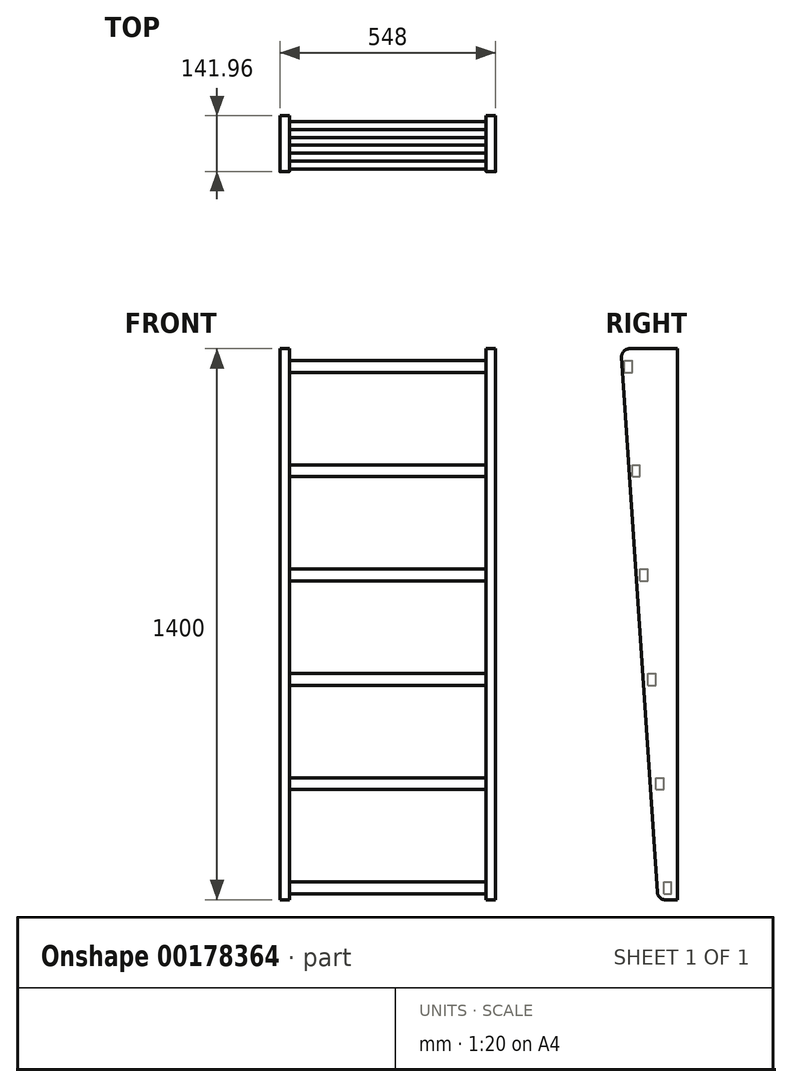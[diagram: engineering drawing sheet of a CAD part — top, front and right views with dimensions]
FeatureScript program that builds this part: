
annotation { "Feature Type Name" : "Feature", "Feature Type Description" : "" }
export const myFeature = defineFeature(function(context is Context, id is Id, definition is map)
    precondition{}
    {
        {
            var Q0;
            Q0=qCreatedBy(makeId("Top.planeOp"),FACE);
            var sketch = newSketch(context, id + "F0", { "sketchPlane" : qUnion([Q0])});
            skLineSegment(sketch, "E0.bottom", {"start": v(-250, -75) * mm, "end": v(-274, -75) * mm});
            skLineSegment(sketch, "E0.top", {"start": v(-250, 75) * mm, "end": v(-274, 75) * mm});
            skLineSegment(sketch, "E0.left", {"start": v(-250, -75) * mm, "end": v(-250, 75) * mm});
            skLineSegment(sketch, "E0.right", {"start": v(-274, -75) * mm, "end": v(-274, 75) * mm});
            skPoint(sketch, "E0.middle", {"position": v(-262, 0) * mm});
            skLineSegment(sketch, "E1.MirrorCS", {"start": v(250, -75) * mm, "end": v(274, -75) * mm});
            skPoint(sketch, "E2.MirrorP", {"position": v(262, 0) * mm});
            skLineSegment(sketch, "E3.MirrorCS", {"start": v(274, -75) * mm, "end": v(274, 75) * mm});
            skLineSegment(sketch, "E4.MirrorCS", {"start": v(250, -75) * mm, "end": v(250, 75) * mm});
            skLineSegment(sketch, "E5.MirrorCS", {"start": v(250, 75) * mm, "end": v(274, 75) * mm});
            skSolve(sketch);
        }
        {
            var Q0;
            Q0 = qSketchRegion(id + "F0", true);
            extrude(context, id + "F1", {"entities" : qUnion([Q0]), "depth" : 1400 * mm});
        }
        {
            var Q0;
            Q0=makeQuery(id+"F1.opExtrude","SWEPT_FACE",FACE,{"disambiguationData":[OSD([sQuery(id+"F0.wireOp",EDGE,"E4.MirrorCS")])]});
            var sketch = newSketch(context, id + "F2", { "sketchPlane" : qUnion([Q0])});
            skPoint(sketch, "E6.centerSnap0", {"position": v(0, 1400) * mm});
            skLineSegment(sketch, "E7.bottom", {"start": v(10, 1340) * mm, "end": v(-10, 1340) * mm});
            skLineSegment(sketch, "E7.top", {"start": v(10, 1370) * mm, "end": v(-10, 1370) * mm});
            skLineSegment(sketch, "E7.left", {"start": v(10, 1340) * mm, "end": v(10, 1370) * mm});
            skLineSegment(sketch, "E7.right", {"start": v(-10, 1340) * mm, "end": v(-10, 1370) * mm});
            skPoint(sketch, "E7.middle", {"position": v(0, 1355) * mm});
            skLineSegment(sketch, "E8.0.1.0", {"start": v(10, 1075) * mm, "end": v(10, 1105) * mm});
            skLineSegment(sketch, "E8.0.1.1", {"start": v(-10, 1075) * mm, "end": v(-10, 1105) * mm});
            skPoint(sketch, "E8.0.1.2", {"position": v(0, 1090) * mm});
            skLineSegment(sketch, "E8.0.1.3", {"start": v(10, 1105) * mm, "end": v(-10, 1105) * mm});
            skLineSegment(sketch, "E8.0.1.4", {"start": v(10, 1075) * mm, "end": v(-10, 1075) * mm});
            skLineSegment(sketch, "E8.0.2.0", {"start": v(10, 810) * mm, "end": v(10, 840) * mm});
            skLineSegment(sketch, "E8.0.2.1", {"start": v(-10, 810) * mm, "end": v(-10, 840) * mm});
            skPoint(sketch, "E8.0.2.2", {"position": v(0, 825) * mm});
            skLineSegment(sketch, "E8.0.2.3", {"start": v(10, 840) * mm, "end": v(-10, 840) * mm});
            skLineSegment(sketch, "E8.0.2.4", {"start": v(10, 810) * mm, "end": v(-10, 810) * mm});
            skLineSegment(sketch, "E8.0.3.0", {"start": v(10, 545) * mm, "end": v(10, 575) * mm});
            skLineSegment(sketch, "E8.0.3.1", {"start": v(-10, 545) * mm, "end": v(-10, 575) * mm});
            skPoint(sketch, "E8.0.3.2", {"position": v(0, 560) * mm});
            skLineSegment(sketch, "E8.0.3.3", {"start": v(10, 575) * mm, "end": v(-10, 575) * mm});
            skLineSegment(sketch, "E8.0.3.4", {"start": v(10, 545) * mm, "end": v(-10, 545) * mm});
            skLineSegment(sketch, "E8.0.4.0", {"start": v(10, 280) * mm, "end": v(10, 310) * mm});
            skLineSegment(sketch, "E8.0.4.1", {"start": v(-10, 280) * mm, "end": v(-10, 310) * mm});
            skPoint(sketch, "E8.0.4.2", {"position": v(0, 295) * mm});
            skLineSegment(sketch, "E8.0.4.3", {"start": v(10, 310) * mm, "end": v(-10, 310) * mm});
            skLineSegment(sketch, "E8.0.4.4", {"start": v(10, 280) * mm, "end": v(-10, 280) * mm});
            skLineSegment(sketch, "E8.direction1", {"start": v(-10, 1340) * mm, "end": v(21, 1340) * mm, "construction": true});
            skLineSegment(sketch, "E8.direction2", {"start": v(-10, 1340) * mm, "end": v(-10, 1075) * mm, "construction": true});
            skLineSegment(sketch, "E9.0.0.5", {"start": v(10, 15) * mm, "end": v(10, 45) * mm});
            skLineSegment(sketch, "E9.3.0.5", {"start": v(-10, 15) * mm, "end": v(-10, 45) * mm});
            skPoint(sketch, "E9.6.0.5", {"position": v(0, 30) * mm});
            skLineSegment(sketch, "E9.7.0.5", {"start": v(10, 45) * mm, "end": v(-10, 45) * mm});
            skLineSegment(sketch, "E9.10.0.5", {"start": v(10, 15) * mm, "end": v(-10, 15) * mm});
            skSolve(sketch);
        }
        {
            var Q0;
            Q0=makeQuery(id+"F2.imprint","IMPRINT",FACE,{"disambiguationData":[TD([[makeQuery(id+"F2.imprint","IMPRINT",EDGE,{"derivedFrom":sQuery(id+"F2.wireOp",EDGE,"E7.bottom")}),-1.0]])]});
            var Q1;
            Q1=makeQuery(id+"F2.imprint","IMPRINT",FACE,{"disambiguationData":[TD([[makeQuery(id+"F2.imprint","IMPRINT",EDGE,{"derivedFrom":sQuery(id+"F2.wireOp",EDGE,"E8.0.1.0")}),1.0]])]});
            var Q2;
            Q2=makeQuery(id+"F2.imprint","IMPRINT",FACE,{"disambiguationData":[TD([[makeQuery(id+"F2.imprint","IMPRINT",EDGE,{"derivedFrom":sQuery(id+"F2.wireOp",EDGE,"E8.0.2.0")}),1.0]])]});
            var Q3;
            Q3=makeQuery(id+"F2.imprint","IMPRINT",FACE,{"disambiguationData":[TD([[makeQuery(id+"F2.imprint","IMPRINT",EDGE,{"derivedFrom":sQuery(id+"F2.wireOp",EDGE,"E8.0.3.0")}),1.0]])]});
            var Q4;
            Q4=makeQuery(id+"F2.imprint","IMPRINT",FACE,{"disambiguationData":[TD([[makeQuery(id+"F2.imprint","IMPRINT",EDGE,{"derivedFrom":sQuery(id+"F2.wireOp",EDGE,"E9.0.0.5")}),1.0]])]});
            var Q5;
            Q5=makeQuery(id+"F2.imprint","IMPRINT",FACE,{"disambiguationData":[TD([[makeQuery(id+"F2.imprint","IMPRINT",EDGE,{"derivedFrom":sQuery(id+"F2.wireOp",EDGE,"E8.0.4.0")}),1.0]])]});
            extrude(context, id + "F3", {"entities" : qUnion([Q0, Q1, Q2, Q3, Q4, Q5]), "endBound" : BoundingType.UP_TO_NEXT, "depth" : 25 * mm});
        }
        {
            var Q0;
            Q0=makeQuery(id+"F1.opExtrude","CAP_EDGE",EDGE,{"disambiguationData":[OSD([sQuery(id+"F0.wireOp",EDGE,"E0.bottom")])],"isStart":true});
            chamfer(context, id + "F4", {"entities" : qUnion([Q0]), "chamferType" : ChamferType.TWO_OFFSETS, "width1" : 100 * mm, "oppositeDirection" : false, "width2" : 1500 * mm, "tangentPropagation" : true});
        }
        {
            var Q0;
            Q0=makeQuery(id+"F1.opExtrude","CAP_EDGE",EDGE,{"disambiguationData":[OSD([sQuery(id+"F0.wireOp",EDGE,"E1.MirrorCS")])],"isStart":true});
            chamfer(context, id + "F5", {"entities" : qUnion([Q0]), "chamferType" : ChamferType.TWO_OFFSETS, "width1" : 1500 * mm, "oppositeDirection" : false, "width2" : 100 * mm, "tangentPropagation" : true});
        }
        {
            var Q0;
            Q0=makeQuery(id+"F3.opExtrude","SWEPT_BODY",BODY,{"disambiguationData":[OSD([sQuery(id+"F2.wireOp",EDGE,"E7.bottom"),sQuery(id+"F2.wireOp",EDGE,"E7.top"),sQuery(id+"F2.wireOp",EDGE,"E7.left"),sQuery(id+"F2.wireOp",EDGE,"E7.right")])]});
            transform(context, id + "F6", {"entities" : qUnion([Q0]), "transformType" : TransformType.TRANSLATION_3D, "dx" : 0 * mm, "dy" : -50 * mm, "dz" : 0 * mm, "makeCopy" : false});
        }
        {
            var Q0;
            Q0=makeQuery(id+"F3.opExtrude","SWEPT_BODY",BODY,{"disambiguationData":[OSD([sQuery(id+"F2.wireOp",EDGE,"E8.0.1.0"),sQuery(id+"F2.wireOp",EDGE,"E8.0.1.1"),sQuery(id+"F2.wireOp",EDGE,"E8.0.1.3"),sQuery(id+"F2.wireOp",EDGE,"E8.0.1.4")])]});
            transform(context, id + "F7", {"entities" : qUnion([Q0]), "transformType" : TransformType.TRANSLATION_3D, "dx" : 0 * mm, "dy" : -30 * mm, "dz" : 0 * mm, "makeCopy" : false});
        }
        {
            var Q0;
            Q0=makeQuery(id+"F3.opExtrude","SWEPT_BODY",BODY,{"disambiguationData":[OSD([sQuery(id+"F2.wireOp",EDGE,"E8.0.2.0"),sQuery(id+"F2.wireOp",EDGE,"E8.0.2.1"),sQuery(id+"F2.wireOp",EDGE,"E8.0.2.3"),sQuery(id+"F2.wireOp",EDGE,"E8.0.2.4")])]});
            transform(context, id + "F8", {"entities" : qUnion([Q0]), "transformType" : TransformType.TRANSLATION_3D, "dx" : 0 * mm, "dy" : -10 * mm, "dz" : 0 * mm, "makeCopy" : false});
        }
        {
            var Q0;
            Q0=makeQuery(id+"F3.opExtrude","SWEPT_BODY",BODY,{"disambiguationData":[OSD([sQuery(id+"F2.wireOp",EDGE,"E8.0.3.0"),sQuery(id+"F2.wireOp",EDGE,"E8.0.3.1"),sQuery(id+"F2.wireOp",EDGE,"E8.0.3.3"),sQuery(id+"F2.wireOp",EDGE,"E8.0.3.4")])]});
            transform(context, id + "F9", {"entities" : qUnion([Q0]), "transformType" : TransformType.TRANSLATION_3D, "dx" : 0 * mm, "dy" : 10 * mm, "dz" : 0 * mm, "makeCopy" : false});
        }
        {
            var Q0;
            Q0=makeQuery(id+"F3.opExtrude","SWEPT_BODY",BODY,{"disambiguationData":[OSD([sQuery(id+"F2.wireOp",EDGE,"E8.0.4.0"),sQuery(id+"F2.wireOp",EDGE,"E8.0.4.1"),sQuery(id+"F2.wireOp",EDGE,"E8.0.4.3"),sQuery(id+"F2.wireOp",EDGE,"E8.0.4.4")])]});
            transform(context, id + "F10", {"entities" : qUnion([Q0]), "transformType" : TransformType.TRANSLATION_3D, "dx" : 0 * mm, "dy" : 30 * mm, "dz" : 0 * mm, "makeCopy" : false});
        }
        {
            var Q0;
            Q0=makeQuery(id+"F3.opExtrude","SWEPT_BODY",BODY,{"disambiguationData":[OSD([sQuery(id+"F2.wireOp",EDGE,"E9.0.0.5"),sQuery(id+"F2.wireOp",EDGE,"E9.3.0.5"),sQuery(id+"F2.wireOp",EDGE,"E9.7.0.5"),sQuery(id+"F2.wireOp",EDGE,"E9.10.0.5")])]});
            transform(context, id + "F11", {"entities" : qUnion([Q0]), "transformType" : TransformType.TRANSLATION_3D, "dx" : 0 * mm, "dy" : 50 * mm, "dz" : 0 * mm, "makeCopy" : false});
        }
        {
            var Q0;
            {var subQ0=sQuery(id+"F0.wireOp",EDGE,"E0.bottom");Q0=makeQuery(id+"F4.opChamfer","BLEND_EDGE",EDGE,{"blendedFrom":[makeQuery(id+"F1.opExtrude","CAP_EDGE",EDGE,{"disambiguationData":[OSD([subQ0])],"isStart":true}),makeQuery(id+"F1.opExtrude","CAP_FACE",FACE,{"disambiguationData":[OSD([subQ0,sQuery(id+"F0.wireOp",EDGE,"E0.top"),sQuery(id+"F0.wireOp",EDGE,"E0.left"),sQuery(id+"F0.wireOp",EDGE,"E0.right")])],"isStart":false})],"blendedInto":[makeQuery(id+"F1.opExtrude","CAP_FACE",FACE,{"disambiguationData":[OSD([subQ0,sQuery(id+"F0.wireOp",EDGE,"E0.top"),sQuery(id+"F0.wireOp",EDGE,"E0.left"),sQuery(id+"F0.wireOp",EDGE,"E0.right")])],"isStart":false})]});}
            var Q1;
            {var subQ0=sQuery(id+"F0.wireOp",EDGE,"E1.MirrorCS");Q1=makeQuery(id+"F5.opChamfer","BLEND_EDGE",EDGE,{"blendedFrom":[makeQuery(id+"F1.opExtrude","CAP_EDGE",EDGE,{"disambiguationData":[OSD([subQ0])],"isStart":true}),makeQuery(id+"F1.opExtrude","CAP_FACE",FACE,{"disambiguationData":[OSD([subQ0,sQuery(id+"F0.wireOp",EDGE,"E3.MirrorCS"),sQuery(id+"F0.wireOp",EDGE,"E4.MirrorCS"),sQuery(id+"F0.wireOp",EDGE,"E5.MirrorCS")])],"isStart":false})],"blendedInto":[makeQuery(id+"F1.opExtrude","CAP_FACE",FACE,{"disambiguationData":[OSD([subQ0,sQuery(id+"F0.wireOp",EDGE,"E3.MirrorCS"),sQuery(id+"F0.wireOp",EDGE,"E4.MirrorCS"),sQuery(id+"F0.wireOp",EDGE,"E5.MirrorCS")])],"isStart":false})]});}
            var Q2;
            {var subQ0=sQuery(id+"F0.wireOp",EDGE,"E1.MirrorCS");Q2=makeQuery(id+"F5.opChamfer","BLEND_EDGE",EDGE,{"blendedFrom":[makeQuery(id+"F1.opExtrude","CAP_EDGE",EDGE,{"disambiguationData":[OSD([subQ0])],"isStart":true}),makeQuery(id+"F1.opExtrude","CAP_FACE",FACE,{"disambiguationData":[OSD([subQ0,sQuery(id+"F0.wireOp",EDGE,"E3.MirrorCS"),sQuery(id+"F0.wireOp",EDGE,"E4.MirrorCS"),sQuery(id+"F0.wireOp",EDGE,"E5.MirrorCS")])],"isStart":true})],"blendedInto":[makeQuery(id+"F1.opExtrude","CAP_FACE",FACE,{"disambiguationData":[OSD([subQ0,sQuery(id+"F0.wireOp",EDGE,"E3.MirrorCS"),sQuery(id+"F0.wireOp",EDGE,"E4.MirrorCS"),sQuery(id+"F0.wireOp",EDGE,"E5.MirrorCS")])],"isStart":true})]});}
            var Q3;
            {var subQ0=sQuery(id+"F0.wireOp",EDGE,"E0.bottom");Q3=makeQuery(id+"F4.opChamfer","BLEND_EDGE",EDGE,{"blendedFrom":[makeQuery(id+"F1.opExtrude","CAP_EDGE",EDGE,{"disambiguationData":[OSD([subQ0])],"isStart":true}),makeQuery(id+"F1.opExtrude","CAP_FACE",FACE,{"disambiguationData":[OSD([subQ0,sQuery(id+"F0.wireOp",EDGE,"E0.top"),sQuery(id+"F0.wireOp",EDGE,"E0.left"),sQuery(id+"F0.wireOp",EDGE,"E0.right")])],"isStart":true})],"blendedInto":[makeQuery(id+"F1.opExtrude","CAP_FACE",FACE,{"disambiguationData":[OSD([subQ0,sQuery(id+"F0.wireOp",EDGE,"E0.top"),sQuery(id+"F0.wireOp",EDGE,"E0.left"),sQuery(id+"F0.wireOp",EDGE,"E0.right")])],"isStart":true})]});}
            fillet(context, id + "F12", {"entities" : qUnion([Q0, Q1, Q2, Q3]), "radius" : 20 * mm, "tangentPropagation" : true, "allowEdgeOverflow" : false});
        }
    });
